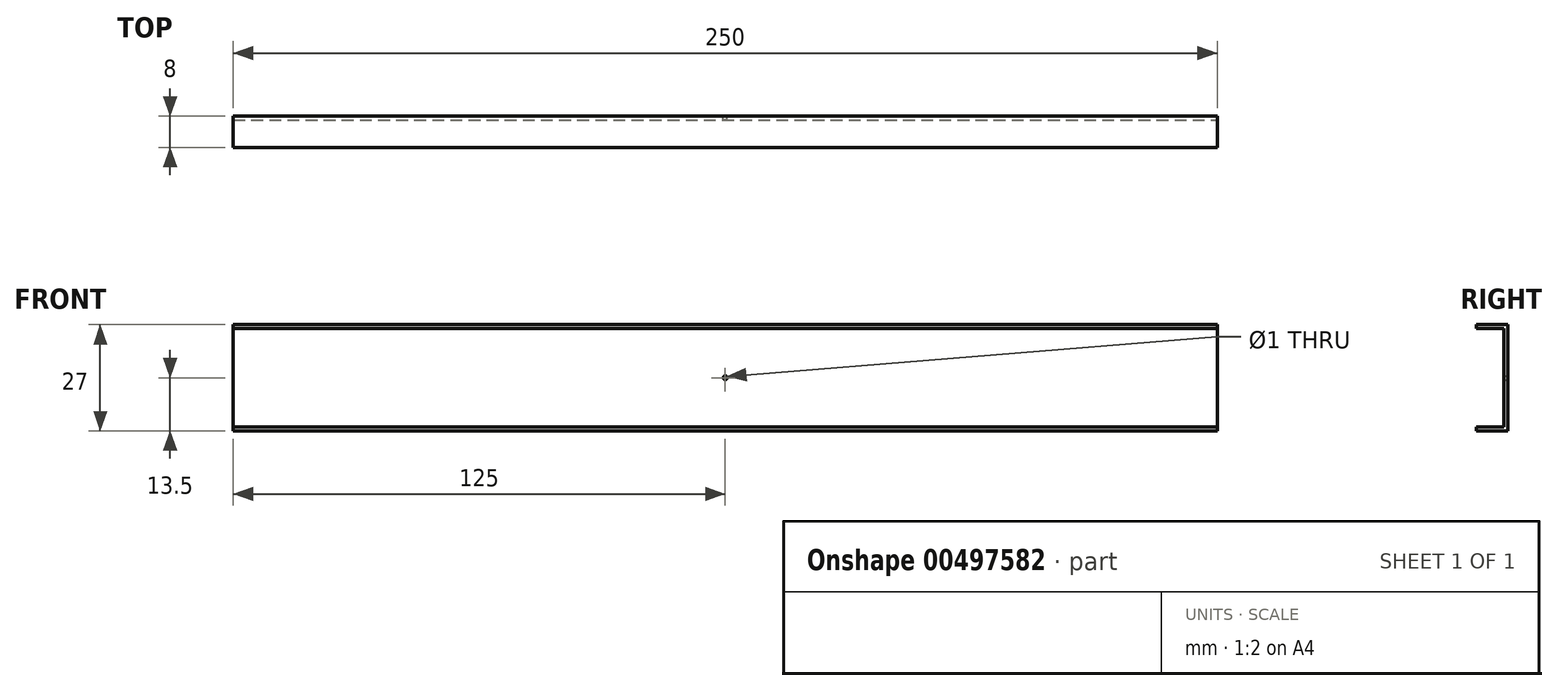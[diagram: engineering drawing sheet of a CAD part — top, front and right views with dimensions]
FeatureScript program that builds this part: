
annotation { "Feature Type Name" : "Feature", "Feature Type Description" : "" }
export const myFeature = defineFeature(function(context is Context, id is Id, definition is map)
    precondition{}
    {
        {
            var Q0;
            Q0=qCreatedBy(makeId("Front.planeOp"),FACE);
            var sketch = newSketch(context, id + "F0", { "sketchPlane" : qUnion([Q0])});
            skLineSegment(sketch, "E0.bottom", {"start": v(0, 0) * mm, "end": v(250, 0) * mm});
            skLineSegment(sketch, "E0.top", {"start": v(0, 27) * mm, "end": v(250, 27) * mm});
            skLineSegment(sketch, "E0.left", {"start": v(0, 0) * mm, "end": v(0, 27) * mm});
            skLineSegment(sketch, "E0.right", {"start": v(250, 0) * mm, "end": v(250, 27) * mm});
            skCircle(sketch, "E1", {"center": v(125, 13.5) * mm, "radius": 0.5 * mm});
            skPoint(sketch, "E1.centerSnap0", {"position": v(125, 0) * mm});
            skPoint(sketch, "E1.centerSnap1", {"position": v(0, 13.5) * mm});
            skSolve(sketch);
        }
        {
            var Q0;
            Q0 = qSketchRegion(id + "F0", true);
            extrude(context, id + "F1", {"entities" : qUnion([Q0]), "depth" : 1 * mm, "offsetDistance" : 25.4 * mm});
        }
        {
            var Q0;
            Q0=makeQuery(id+"F1.opExtrude","CAP_FACE",FACE,{"disambiguationData":[OSD([sQuery(id+"F0.wireOp",EDGE,"E0.bottom"),sQuery(id+"F0.wireOp",EDGE,"E0.top"),sQuery(id+"F0.wireOp",EDGE,"E0.left"),sQuery(id+"F0.wireOp",EDGE,"E0.right")])],"isStart":false});
            var sketch = newSketch(context, id + "F2", { "sketchPlane" : qUnion([Q0])});
            skLineSegment(sketch, "E2.bottom", {"start": v(0, 27) * mm, "end": v(250, 27) * mm});
            skLineSegment(sketch, "E2.top", {"start": v(0, 26) * mm, "end": v(250, 26) * mm});
            skLineSegment(sketch, "E2.left", {"start": v(0, 27) * mm, "end": v(0, 26) * mm});
            skLineSegment(sketch, "E2.right", {"start": v(250, 27) * mm, "end": v(250, 26) * mm});
            skLineSegment(sketch, "E3", {"start": v(0, 13.5) * mm, "end": v(250, 13.5) * mm, "construction": true});
            skLineSegment(sketch, "E4.MirrorCS", {"start": v(0, 0) * mm, "end": v(0, 1) * mm});
            skLineSegment(sketch, "E5.MirrorCS", {"start": v(250, 0) * mm, "end": v(250, 1) * mm});
            skLineSegment(sketch, "E6.MirrorCS", {"start": v(0, 0) * mm, "end": v(250, 0) * mm});
            skLineSegment(sketch, "E7.MirrorCS", {"start": v(0, 1) * mm, "end": v(250, 1) * mm});
            skSolve(sketch);
        }
        {
            var Q0;
            Q0 = qSketchRegion(id + "F2", true);
            extrude(context, id + "F3", {"entities" : qUnion([Q0]), "operationType" : NewBodyOperationType.ADD, "depth" : 7 * mm, "offsetDistance" : 25.4 * mm});
        }
    });
